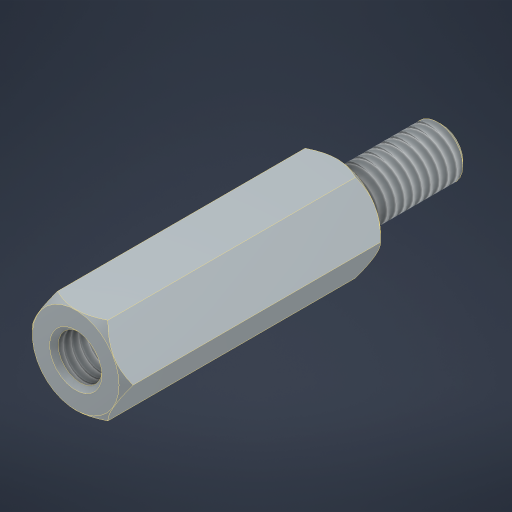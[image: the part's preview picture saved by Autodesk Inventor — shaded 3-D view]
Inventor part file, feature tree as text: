
AUTODESK INVENTOR PART (.ipt)
format: ipt  version: 2023 (Build 270158000, 158)  size: 241,664 bytes
history: native  units: mm
features: thread x2, other x1
ambient origin geometry x8: Origin, YZ Plane, XZ Plane, XY Plane, X Axis, Y Axis, Z Axis, Center Point
bodies: Solid1 (feature_tree)
feature tree (3):
  thread  "Thread1"  [1 undecoded]
  thread  "Thread2"  [1 undecoded]
  other  "InnerChamfer"
note: 2 required parameter values undecoded (feature->parameter linkage not recoverable at this tier; creation-order binding heuristic only, values carry confidence <= 0.55)
